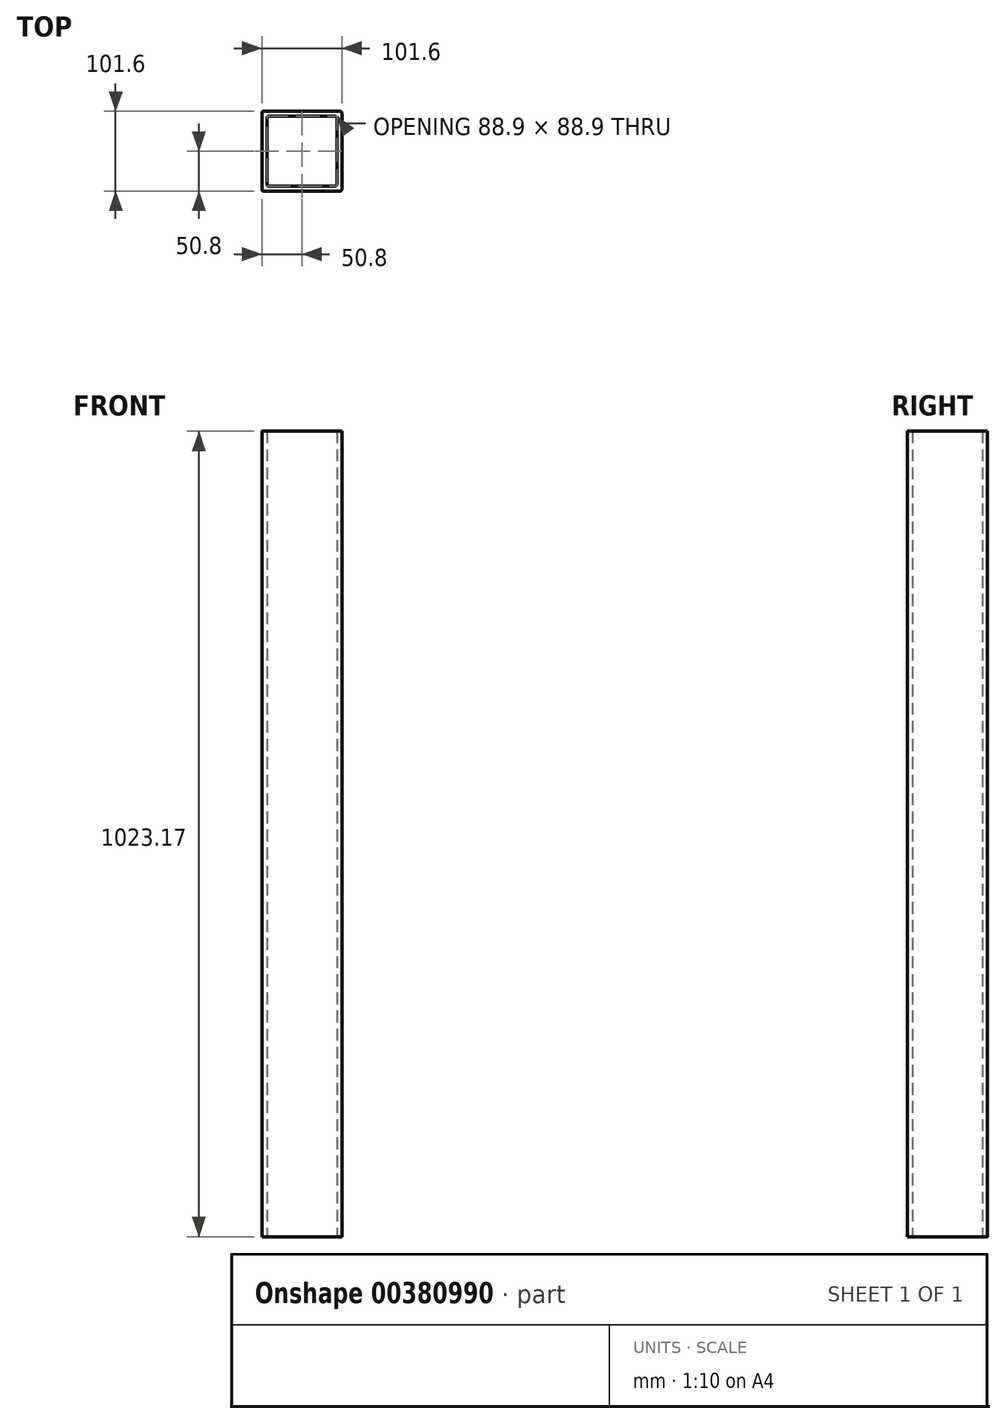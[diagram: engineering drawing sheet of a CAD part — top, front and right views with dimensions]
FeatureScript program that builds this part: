
annotation { "Feature Type Name" : "Feature", "Feature Type Description" : "" }
export const myFeature = defineFeature(function(context is Context, id is Id, definition is map)
    precondition{}
    {
        {
            var Q0;
            Q0=qCreatedBy(makeId("Top.planeOp"),FACE);
            var sketch = newSketch(context, id + "F0", { "sketchPlane" : qUnion([Q0])});
            skLineSegment(sketch, "E0.bottom", {"start": v(50.8, 50.8) * mm, "end": v(-50.8, 50.8) * mm});
            skLineSegment(sketch, "E0.top", {"start": v(50.8, -50.8) * mm, "end": v(-50.8, -50.8) * mm});
            skLineSegment(sketch, "E0.left", {"start": v(50.8, 50.8) * mm, "end": v(50.8, -50.8) * mm});
            skLineSegment(sketch, "E0.right", {"start": v(-50.8, 50.8) * mm, "end": v(-50.8, -50.8) * mm});
            skPoint(sketch, "E0.middle", {"position": v(0, 0) * mm});
            skLineSegment(sketch, "E1.bottom", {"start": v(44.45, 44.45) * mm, "end": v(-44.45, 44.45) * mm});
            skLineSegment(sketch, "E1.top", {"start": v(44.45, -44.45) * mm, "end": v(-44.45, -44.45) * mm});
            skLineSegment(sketch, "E1.left", {"start": v(44.45, 44.45) * mm, "end": v(44.45, -44.45) * mm});
            skLineSegment(sketch, "E1.right", {"start": v(-44.45, 44.45) * mm, "end": v(-44.45, -44.45) * mm});
            skSolve(sketch);
        }
        {
            var Q0;
            Q0=makeQuery(id+"F0.imprint","IMPRINT",FACE,{"disambiguationData":[TD([[makeQuery(id+"F0.imprint","IMPRINT",EDGE,{"derivedFrom":sQuery(id+"F0.wireOp",EDGE,"E0.bottom")}),1.0]])]});
            extrude(context, id + "F1", {"entities" : qUnion([Q0]), "depth" : 1023.17 * mm});
        }
        {
            var Q0;
            Q0=makeQuery(id+"F1.opExtrude","SWEPT_EDGE",EDGE,{"disambiguationData":[OSD([sQuery(id+"F0.wireOp",EDGE,"E0.top"),sQuery(id+"F0.wireOp",EDGE,"E0.left")])]});
            var Q1;
            Q1=makeQuery(id+"F1.opExtrude","SWEPT_EDGE",EDGE,{"disambiguationData":[OSD([sQuery(id+"F0.wireOp",EDGE,"E0.bottom"),sQuery(id+"F0.wireOp",EDGE,"E0.left")])]});
            var Q2;
            Q2=makeQuery(id+"F1.opExtrude","SWEPT_EDGE",EDGE,{"disambiguationData":[OSD([sQuery(id+"F0.wireOp",EDGE,"E0.bottom"),sQuery(id+"F0.wireOp",EDGE,"E0.right")])]});
            var Q3;
            Q3=makeQuery(id+"F1.opExtrude","SWEPT_EDGE",EDGE,{"disambiguationData":[OSD([sQuery(id+"F0.wireOp",EDGE,"E0.top"),sQuery(id+"F0.wireOp",EDGE,"E0.right")])]});
            var Q4;
            Q4=makeQuery(id+"F1.opExtrude","SWEPT_EDGE",EDGE,{"disambiguationData":[OSD([sQuery(id+"F0.wireOp",EDGE,"E1.top"),sQuery(id+"F0.wireOp",EDGE,"E1.left")])]});
            var Q5;
            Q5=makeQuery(id+"F1.opExtrude","SWEPT_EDGE",EDGE,{"disambiguationData":[OSD([sQuery(id+"F0.wireOp",EDGE,"E1.top"),sQuery(id+"F0.wireOp",EDGE,"E1.right")])]});
            var Q6;
            Q6=makeQuery(id+"F1.opExtrude","SWEPT_EDGE",EDGE,{"disambiguationData":[OSD([sQuery(id+"F0.wireOp",EDGE,"E1.bottom"),sQuery(id+"F0.wireOp",EDGE,"E1.right")])]});
            var Q7;
            Q7=makeQuery(id+"F1.opExtrude","SWEPT_EDGE",EDGE,{"disambiguationData":[OSD([sQuery(id+"F0.wireOp",EDGE,"E1.bottom"),sQuery(id+"F0.wireOp",EDGE,"E1.left")])]});
            fillet(context, id + "F2", {"entities" : qUnion([Q0, Q1, Q2, Q3, Q4, Q5, Q6, Q7]), "radius" : 2.5 * mm, "tangentPropagation" : true, "allowEdgeOverflow" : false});
        }
    });
